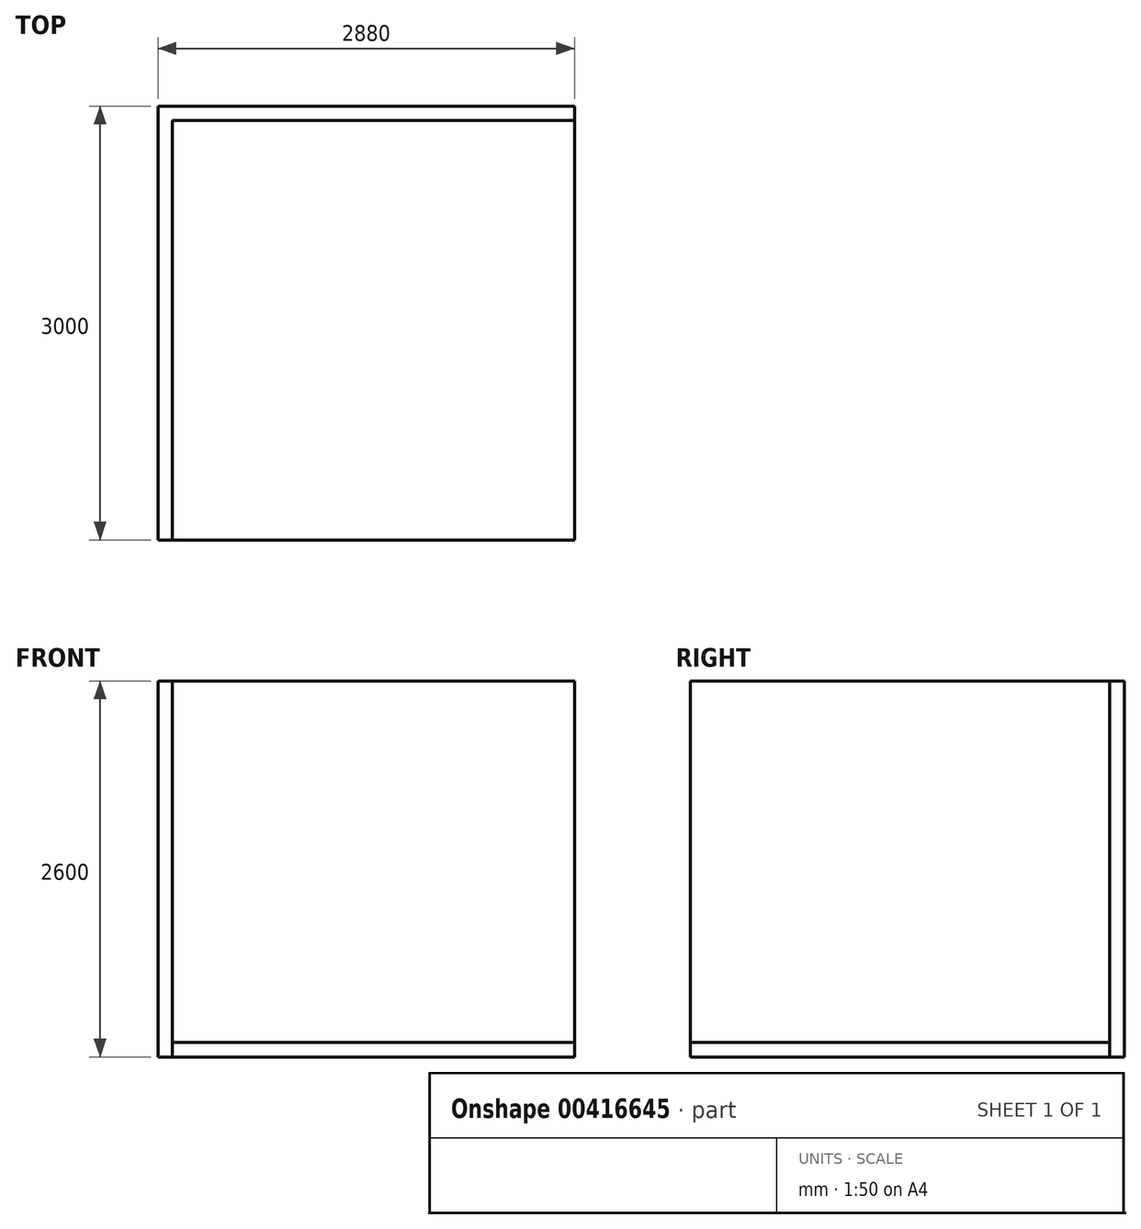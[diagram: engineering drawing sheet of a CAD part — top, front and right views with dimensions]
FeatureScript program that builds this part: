
annotation { "Feature Type Name" : "Feature", "Feature Type Description" : "" }
export const myFeature = defineFeature(function(context is Context, id is Id, definition is map)
    precondition{}
    {
        {
            var Q0;
            Q0=qCreatedBy(makeId("Front.planeOp"),FACE);
            var sketch = newSketch(context, id + "F0", { "sketchPlane" : qUnion([Q0])});
            skLineSegment(sketch, "E0", {"start": v(0, 0) * mm, "end": v(0, 2600) * mm});
            skLineSegment(sketch, "E1", {"start": v(0, 2600) * mm, "end": v(100, 2600) * mm});
            skLineSegment(sketch, "E2", {"start": v(100, 2600) * mm, "end": v(100, 0) * mm});
            skLineSegment(sketch, "E3", {"start": v(100, 0) * mm, "end": v(0, 0) * mm});
            skSolve(sketch);
        }
        {
            var Q0;
            Q0 = qSketchRegion(id + "F0", true);
            var Q1;
            Q1=makeQuery(id+"F0.imprint","IMPRINT",FACE,{"disambiguationData":[TD([[makeQuery(id+"F0.imprint","IMPRINT",EDGE,{"derivedFrom":sQuery(id+"F0.wireOp",EDGE,"E0")}),-1.0]])]});
            extrude(context, id + "F1", {"entities" : qUnion([Q0, Q1]), "depth" : 3000 * mm});
        }
        {
            var Q0;
            Q0=makeQuery(id+"F1.opExtrude","SWEPT_FACE",FACE,{"disambiguationData":[OSD([sQuery(id+"F0.wireOp",EDGE,"E2")])]});
            var sketch = newSketch(context, id + "F2", { "sketchPlane" : qUnion([Q0])});
            skLineSegment(sketch, "E4", {"start": v(0, 0) * mm, "end": v(0, 2600) * mm});
            skLineSegment(sketch, "E5", {"start": v(0, 2600) * mm, "end": v(-100, 2600) * mm});
            skLineSegment(sketch, "E6", {"start": v(-100, 2600) * mm, "end": v(-100, 0) * mm});
            skLineSegment(sketch, "E7", {"start": v(-100, 0) * mm, "end": v(0, 0) * mm});
            skSolve(sketch);
        }
        {
            var Q0;
            Q0=makeQuery(id+"F2.imprint","IMPRINT",FACE,{"disambiguationData":[TD([[makeQuery(id+"F2.imprint","IMPRINT",EDGE,{"derivedFrom":sQuery(id+"F2.wireOp",EDGE,"E4")}),-1.0]])]});
            extrude(context, id + "F3", {"entities" : qUnion([Q0]), "operationType" : NewBodyOperationType.ADD, "depth" : 2780 * mm});
        }
        {
            var Q0;
            Q0=makeQuery(id+"F3.boolean.opBoolean","MERGE",FACE,{"derivedFrom":[makeQuery(id+"F1.opExtrude","SWEPT_FACE",FACE,{"disambiguationData":[OSD([sQuery(id+"F0.wireOp",EDGE,"E3")])]}),makeQuery(id+"F3.opExtrude","SWEPT_FACE",FACE,{"disambiguationData":[OSD([sQuery(id+"F2.wireOp",EDGE,"E7")])]})]});
            var sketch = newSketch(context, id + "F4", { "sketchPlane" : qUnion([Q0])});
            skLineSegment(sketch, "E8", {"start": v(0, 3000) * mm, "end": v(3223.08, 3000) * mm});
            skLineSegment(sketch, "E9", {"start": v(2880, 0) * mm, "end": v(2880, 3000) * mm});
            skLineSegment(sketch, "E10", {"start": v(0, 3000) * mm, "end": v(0, 0) * mm});
            skLineSegment(sketch, "E11", {"start": v(0, 0) * mm, "end": v(2880, 0) * mm});
            skSolve(sketch);
        }
        {
            var Q0;
            {var subQ1=sQuery(id+"F0.wireOp",EDGE,"E3");var subQ2=sQuery(id+"F0.wireOp",EDGE,"E2");var subQ3=makeQuery(id+"F1.opExtrude","SWEPT_EDGE",EDGE,{"disambiguationData":[OSD([subQ2,subQ1])]});Q0=makeQuery(id+"F4.imprint","IMPRINT",FACE,{"disambiguationData":[TD([[makeQuery(id+"F4.imprint","IMPRINT",EDGE,{"derivedFrom":subQ3}),1.0]])]});}
            extrude(context, id + "F5", {"entities" : qUnion([Q0]), "oppositeDirection" : true, "depth" : 100 * mm});
        }
    });
